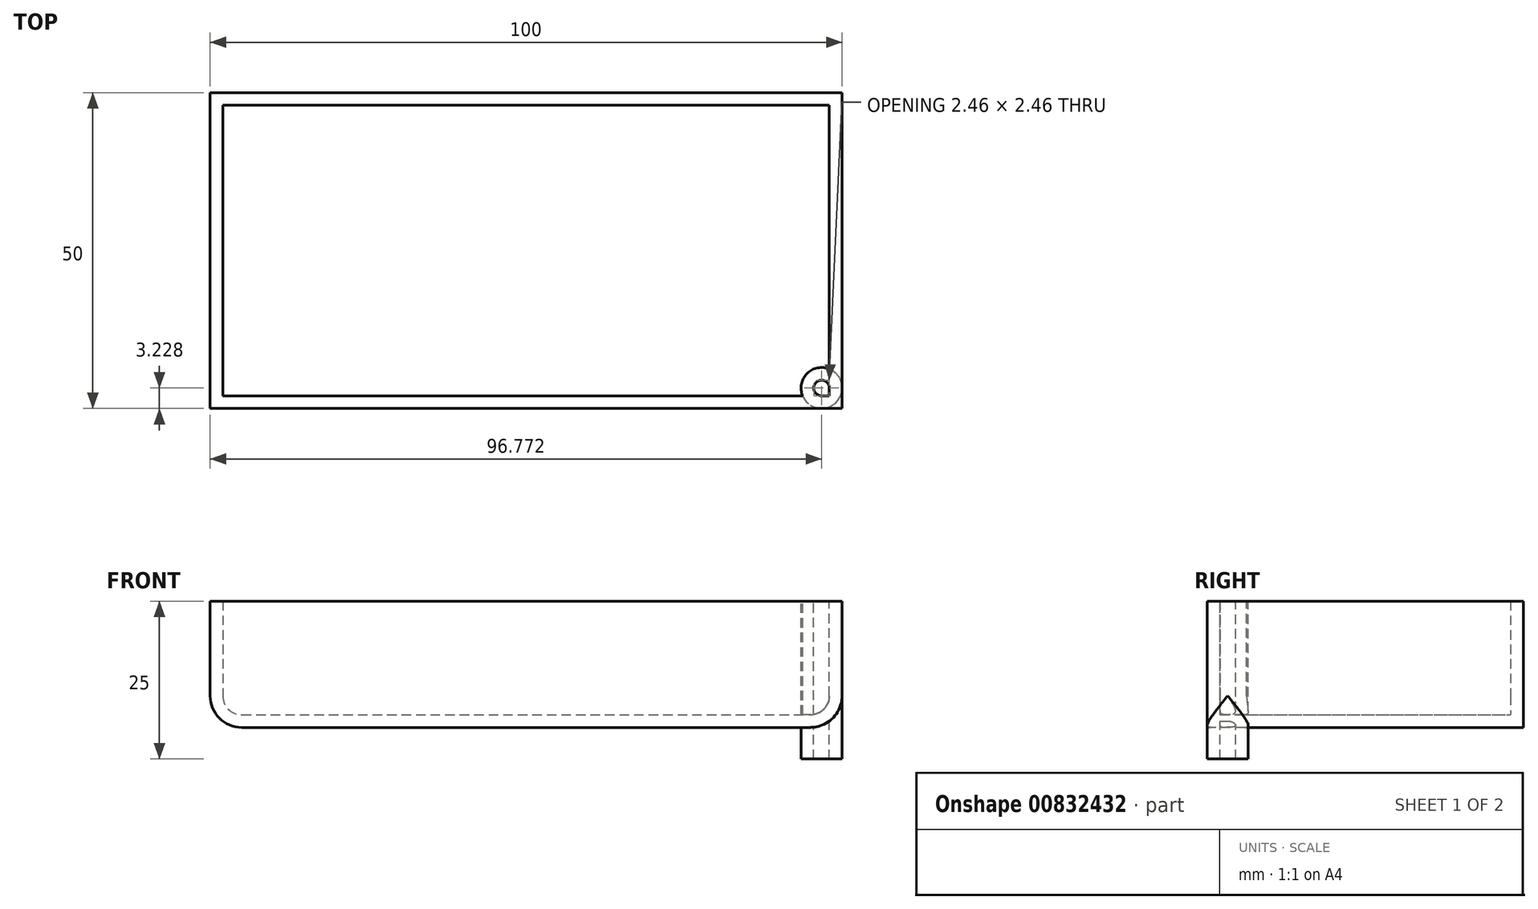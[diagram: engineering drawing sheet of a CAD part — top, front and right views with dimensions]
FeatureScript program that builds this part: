
annotation { "Feature Type Name" : "Feature", "Feature Type Description" : "" }
export const myFeature = defineFeature(function(context is Context, id is Id, definition is map)
    precondition{}
    {
        {
            var Q0;
            Q0=qCreatedBy(makeId("Front.planeOp"),FACE);
            var sketch = newSketch(context, id + "F0", { "sketchPlane" : qUnion([Q0])});
            skLineSegment(sketch, "E0.bottom", {"start": v(-50, 10) * mm, "end": v(50, 10) * mm});
            skLineSegment(sketch, "E0.top", {"start": v(-45, -10) * mm, "end": v(45, -10) * mm});
            skLineSegment(sketch, "E0.left", {"start": v(-50, 10) * mm, "end": v(-50, -5) * mm});
            skLineSegment(sketch, "E0.right", {"start": v(50, 10) * mm, "end": v(50, -5) * mm});
            skPoint(sketch, "E1.visualSharp", {"position": v(-50, -10) * mm});
            skArc(sketch, "E1.filletArc", {"start": v(-50, -5) * mm, "mid": v(-48.54, -8.54) * mm, "end": v(-45, -10) * mm});
            skPoint(sketch, "E2.visualSharp", {"position": v(50, -10) * mm});
            skArc(sketch, "E2.filletArc", {"start": v(45, -10) * mm, "mid": v(48.54, -8.54) * mm, "end": v(50, -5) * mm});
            skSolve(sketch);
        }
        {
            var Q0;
            Q0=makeQuery(id+"F0.imprint","IMPRINT",FACE,{"disambiguationData":[TD([[makeQuery(id+"F0.imprint","IMPRINT",EDGE,{"derivedFrom":sQuery(id+"F0.wireOp",EDGE,"E0.bottom")}),-1.0]])]});
            extrude(context, id + "F1", {"entities" : qUnion([Q0]), "endBound" : BoundingType.SYMMETRIC, "depth" : 50 * mm, "offsetDistance" : 25 * mm});
        }
        {
            var Q0;
            Q0=makeQuery(id+"F1.opExtrude","SWEPT_FACE",FACE,{"disambiguationData":[OSD([sQuery(id+"F0.wireOp",EDGE,"E0.bottom")])]});
            shell(context, id + "F2", {"entities" : qUnion([Q0]), "thickness" : 2 * mm});
        }
        {
            var Q0;
            Q0=makeQuery(id+"F1.opExtrude","SWEPT_FACE",FACE,{"disambiguationData":[OSD([sQuery(id+"F0.wireOp",EDGE,"E0.bottom")])]});
            var sketch = newSketch(context, id + "F3", { "sketchPlane" : qUnion([Q0])});
            skCircle(sketch, "E3", {"center": v(46.76, -21.76) * mm, "radius": 1.24 * mm});
            skCircle(sketch, "E4", {"center": v(46.76, -21.76) * mm, "radius": 3.24 * mm});
            skSolve(sketch);
        }
        {
            var Q0;
            {var subQ0=sQuery(id+"F0.wireOp",EDGE,"E0.bottom");var subQ1=makeQuery(id+"F1.opExtrude","CAP_EDGE",EDGE,{"disambiguationData":[OSD([subQ0])],"isStart":false});var subQ8=sQuery(id+"F3.wireOp",EDGE,"E4");var subQ9=makeQuery(id+"F3.imprint","INTERSECT",VERTEX,{"derivedFrom":[subQ1,subQ8]});Q0=makeQuery(id+"F3.imprint","IMPRINT",FACE,{"disambiguationData":[TD([[makeQuery(id+"F3.imprint","IMPRINT",EDGE,{"disambiguationData":[TD([[subQ9,1.0]])],"derivedFrom":subQ8}),1.0]])]});}
            var Q1;
            {var subQ1=sQuery(id+"F0.wireOp",EDGE,"E0.bottom");var subQ4=makeQuery(id+"F2.opShell","OFFSET_EDGE",EDGE,{"disambiguationData":[OSD([subQ1]),TDD([makeQuery(id+"F1.opExtrude","CAP_EDGE",EDGE,{"disambiguationData":[OSD([subQ1])],"isStart":false})])]});var subQ6=sQuery(id+"F3.wireOp",EDGE,"E4");var subQ8=makeQuery(id+"F3.imprint","INTERSECT",VERTEX,{"derivedFrom":[subQ4,subQ6]});Q1=makeQuery(id+"F3.imprint","IMPRINT",FACE,{"disambiguationData":[TD([[makeQuery(id+"F3.imprint","IMPRINT",EDGE,{"disambiguationData":[TD([[subQ8,-1.0]])],"derivedFrom":subQ4}),1.0]])]});}
            extrude(context, id + "F4", {"entities" : qUnion([Q0, Q1]), "operationType" : NewBodyOperationType.ADD, "oppositeDirection" : true, "depth" : 25 * mm, "offsetDistance" : 25 * mm});
        }
    });
